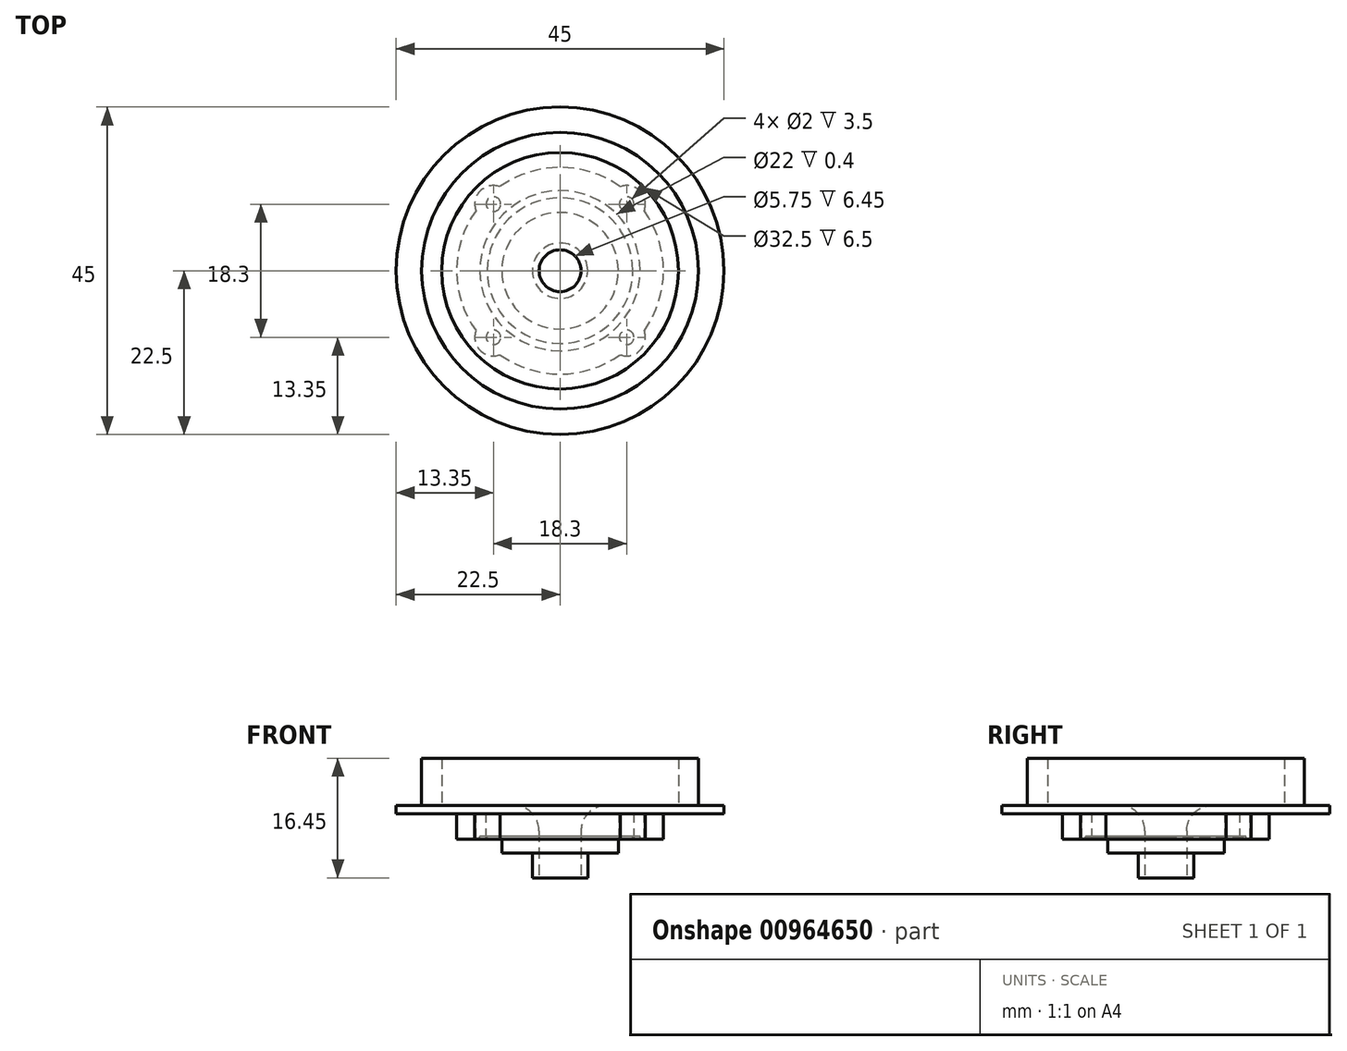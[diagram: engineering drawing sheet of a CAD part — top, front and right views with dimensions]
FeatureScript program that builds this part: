
annotation { "Feature Type Name" : "Feature", "Feature Type Description" : "" }
export const myFeature = defineFeature(function(context is Context, id is Id, definition is map)
    precondition{}
    {
        {
            var Q0;
            Q0=qCreatedBy(makeId("Top.planeOp"),FACE);
            var sketch = newSketch(context, id + "F0", { "sketchPlane" : qUnion([Q0])});
            skCircle(sketch, "E0", {"center": v(0, 0) * mm, "radius": 22.5 * mm});
            skCircle(sketch, "E1", {"center": v(0, 0) * mm, "radius": 19 * mm});
            skCircle(sketch, "E2", {"center": v(0, 0) * mm, "radius": 16.25 * mm});
            skCircle(sketch, "E3", {"center": v(0, 0) * mm, "radius": 6.4 * mm});
            skArc(sketch, "E4", {"start": v(-8.26, -11.55) * mm, "mid": v(0, -14.2) * mm, "end": v(8.26, -11.55) * mm});
            skCircle(sketch, "E5", {"center": v(0, 0) * mm, "radius": 11 * mm});
            skCircle(sketch, "E6", {"center": v(0, 0) * mm, "radius": 10 * mm});
            skCircle(sketch, "E7", {"center": v(0, 0) * mm, "radius": 8 * mm});
            skCircle(sketch, "E8", {"center": v(0, 0) * mm, "radius": 3.8 * mm});
            skCircle(sketch, "E9", {"center": v(0, 0) * mm, "radius": 2.88 * mm});
            skLineSegment(sketch, "E10.bottom", {"start": v(9.15, 9.15) * mm, "end": v(-9.15, 9.15) * mm, "construction": true});
            skLineSegment(sketch, "E10.top", {"start": v(9.15, -9.15) * mm, "end": v(-9.15, -9.15) * mm, "construction": true});
            skLineSegment(sketch, "E10.left", {"start": v(9.15, 9.15) * mm, "end": v(9.15, -9.15) * mm, "construction": true});
            skLineSegment(sketch, "E10.right", {"start": v(-9.15, 9.15) * mm, "end": v(-9.15, -9.15) * mm, "construction": true});
            skCircle(sketch, "E11", {"center": v(-9.15, 9.15) * mm, "radius": 1 * mm});
            skCircle(sketch, "E12", {"center": v(9.15, 9.15) * mm, "radius": 1 * mm});
            skCircle(sketch, "E13", {"center": v(9.15, -9.15) * mm, "radius": 1 * mm});
            skCircle(sketch, "E14", {"center": v(-9.15, -9.15) * mm, "radius": 1 * mm});
            skLineSegment(sketch, "E15.bottom", {"start": v(10.96, 10.96) * mm, "end": v(-10.96, 10.96) * mm, "construction": true});
            skLineSegment(sketch, "E15.top", {"start": v(10.96, -10.96) * mm, "end": v(-10.96, -10.96) * mm, "construction": true});
            skLineSegment(sketch, "E15.left", {"start": v(10.96, 10.96) * mm, "end": v(10.96, -10.96) * mm, "construction": true});
            skLineSegment(sketch, "E15.right", {"start": v(-10.96, 10.96) * mm, "end": v(-10.96, -10.96) * mm, "construction": true});
            skLineSegment(sketch, "E16", {"start": v(-10.96, 10.96) * mm, "end": v(10.96, -10.96) * mm, "construction": true});
            skArc(sketch, "E17", {"start": v(-8.26, 11.55) * mm, "mid": v(-10.96, 10.96) * mm, "end": v(-11.55, 8.26) * mm});
            skArc(sketch, "E18", {"start": v(11.55, 8.26) * mm, "mid": v(10.96, 10.96) * mm, "end": v(8.26, 11.55) * mm});
            skArc(sketch, "E19", {"start": v(8.26, -11.55) * mm, "mid": v(10.96, -10.96) * mm, "end": v(11.55, -8.26) * mm});
            skArc(sketch, "E20.trimOffspring", {"start": v(-11.55, -8.26) * mm, "mid": v(-10.96, -10.96) * mm, "end": v(-8.26, -11.55) * mm});
            skArc(sketch, "E21.trimOffspring", {"start": v(11.55, -8.26) * mm, "mid": v(14.2, 0) * mm, "end": v(11.55, 8.26) * mm});
            skArc(sketch, "E22.trimOffspring", {"start": v(8.26, 11.55) * mm, "mid": v(0, 14.2) * mm, "end": v(-8.26, 11.55) * mm});
            skArc(sketch, "E23.trimOffspring", {"start": v(-11.55, 8.26) * mm, "mid": v(-14.2, 0) * mm, "end": v(-11.55, -8.26) * mm});
            skSolve(sketch);
        }
        {
            var Q0;
            Q0=makeQuery(id+"F0.imprint","IMPRINT",FACE,{"disambiguationData":[TD([[makeQuery(id+"F0.imprint","IMPRINT",EDGE,{"derivedFrom":sQuery(id+"F0.wireOp",EDGE,"E0")}),1.0]])]});
            var Q1;
            Q1=makeQuery(id+"F0.imprint","IMPRINT",FACE,{"disambiguationData":[TD([[makeQuery(id+"F0.imprint","IMPRINT",EDGE,{"derivedFrom":sQuery(id+"F0.wireOp",EDGE,"E1")}),1.0]])]});
            var Q2;
            Q2=makeQuery(id+"F0.imprint","IMPRINT",FACE,{"disambiguationData":[TD([[makeQuery(id+"F0.imprint","IMPRINT",EDGE,{"derivedFrom":sQuery(id+"F0.wireOp",EDGE,"E2")}),1.0]])]});
            var Q3;
            Q3=makeQuery(id+"F0.imprint","IMPRINT",FACE,{"disambiguationData":[TD([[makeQuery(id+"F0.imprint","IMPRINT",EDGE,{"derivedFrom":sQuery(id+"F0.wireOp",EDGE,"E4")}),1.0]])]});
            var Q4;
            Q4=makeQuery(id+"F0.imprint","IMPRINT",FACE,{"disambiguationData":[TD([[makeQuery(id+"F0.imprint","IMPRINT",EDGE,{"derivedFrom":sQuery(id+"F0.wireOp",EDGE,"E5")}),1.0]])]});
            var Q5;
            Q5=makeQuery(id+"F0.imprint","IMPRINT",FACE,{"disambiguationData":[TD([[makeQuery(id+"F0.imprint","IMPRINT",EDGE,{"derivedFrom":sQuery(id+"F0.wireOp",EDGE,"E6")}),1.0]])]});
            var Q6;
            Q6=makeQuery(id+"F0.imprint","IMPRINT",FACE,{"disambiguationData":[TD([[makeQuery(id+"F0.imprint","IMPRINT",EDGE,{"derivedFrom":sQuery(id+"F0.wireOp",EDGE,"E3")}),-1.0]])]});
            var Q7;
            Q7=makeQuery(id+"F0.imprint","IMPRINT",FACE,{"disambiguationData":[TD([[makeQuery(id+"F0.imprint","IMPRINT",EDGE,{"derivedFrom":sQuery(id+"F0.wireOp",EDGE,"E11")}),1.0]])]});
            var Q8;
            Q8=makeQuery(id+"F0.imprint","IMPRINT",FACE,{"disambiguationData":[TD([[makeQuery(id+"F0.imprint","IMPRINT",EDGE,{"derivedFrom":sQuery(id+"F0.wireOp",EDGE,"E12")}),1.0]])]});
            var Q9;
            Q9=makeQuery(id+"F0.imprint","IMPRINT",FACE,{"disambiguationData":[TD([[makeQuery(id+"F0.imprint","IMPRINT",EDGE,{"derivedFrom":sQuery(id+"F0.wireOp",EDGE,"E13")}),1.0]])]});
            var Q10;
            Q10=makeQuery(id+"F0.imprint","IMPRINT",FACE,{"disambiguationData":[TD([[makeQuery(id+"F0.imprint","IMPRINT",EDGE,{"derivedFrom":sQuery(id+"F0.wireOp",EDGE,"E14")}),1.0]])]});
            var Q11;
            Q11=makeQuery(id+"F0.imprint","IMPRINT",FACE,{"disambiguationData":[TD([[makeQuery(id+"F0.imprint","IMPRINT",EDGE,{"derivedFrom":sQuery(id+"F0.wireOp",EDGE,"E3")}),1.0]])]});
            var Q12;
            Q12=makeQuery(id+"F0.imprint","IMPRINT",FACE,{"disambiguationData":[TD([[makeQuery(id+"F0.imprint","IMPRINT",EDGE,{"derivedFrom":sQuery(id+"F0.wireOp",EDGE,"E8")}),1.0]])]});
            extrude(context, id + "F1", {"entities" : qUnion([Q0, Q1, Q2, Q3, Q4, Q5, Q6, Q7, Q8, Q9, Q10, Q11, Q12]), "depth" : 1.15 * mm, "offsetDistance" : 25 * mm});
        }
        {
            var Q0;
            Q0=makeQuery(id+"F0.imprint","IMPRINT",FACE,{"disambiguationData":[TD([[makeQuery(id+"F0.imprint","IMPRINT",EDGE,{"derivedFrom":sQuery(id+"F0.wireOp",EDGE,"E1")}),1.0]])]});
            extrude(context, id + "F2", {"entities" : qUnion([Q0]), "operationType" : NewBodyOperationType.ADD, "depth" : 7.65 * mm, "offsetDistance" : 25 * mm});
        }
        {
            var Q0;
            Q0=makeQuery(id+"F0.imprint","IMPRINT",FACE,{"disambiguationData":[TD([[makeQuery(id+"F0.imprint","IMPRINT",EDGE,{"derivedFrom":sQuery(id+"F0.wireOp",EDGE,"E4")}),1.0]])]});
            var Q1;
            Q1=makeQuery(id+"F0.imprint","IMPRINT",FACE,{"disambiguationData":[TD([[makeQuery(id+"F0.imprint","IMPRINT",EDGE,{"derivedFrom":sQuery(id+"F0.wireOp",EDGE,"E6")}),1.0]])]});
            extrude(context, id + "F3", {"entities" : qUnion([Q0, Q1]), "operationType" : NewBodyOperationType.ADD, "oppositeDirection" : true, "depth" : 3.5 * mm, "offsetDistance" : 25 * mm});
        }
        {
            var Q0;
            Q0=makeQuery(id+"F0.imprint","IMPRINT",FACE,{"disambiguationData":[TD([[makeQuery(id+"F0.imprint","IMPRINT",EDGE,{"derivedFrom":sQuery(id+"F0.wireOp",EDGE,"E5")}),1.0]])]});
            extrude(context, id + "F4", {"entities" : qUnion([Q0]), "operationType" : NewBodyOperationType.ADD, "oppositeDirection" : true, "depth" : 3.1 * mm, "offsetDistance" : 25 * mm});
        }
        {
            var Q0;
            Q0=makeQuery(id+"F0.imprint","IMPRINT",FACE,{"disambiguationData":[TD([[makeQuery(id+"F0.imprint","IMPRINT",EDGE,{"derivedFrom":sQuery(id+"F0.wireOp",EDGE,"E3")}),-1.0]])]});
            var Q1;
            Q1=makeQuery(id+"F0.imprint","IMPRINT",FACE,{"disambiguationData":[TD([[makeQuery(id+"F0.imprint","IMPRINT",EDGE,{"derivedFrom":sQuery(id+"F0.wireOp",EDGE,"E3")}),1.0]])]});
            extrude(context, id + "F5", {"entities" : qUnion([Q0, Q1]), "operationType" : NewBodyOperationType.ADD, "oppositeDirection" : true, "depth" : 5.4 * mm, "offsetDistance" : 25 * mm});
        }
        {
            var Q0;
            Q0=makeQuery(id+"F0.imprint","IMPRINT",FACE,{"disambiguationData":[TD([[makeQuery(id+"F0.imprint","IMPRINT",EDGE,{"derivedFrom":sQuery(id+"F0.wireOp",EDGE,"E8")}),1.0]])]});
            extrude(context, id + "F6", {"entities" : qUnion([Q0]), "operationType" : NewBodyOperationType.ADD, "oppositeDirection" : true, "depth" : 8.8 * mm, "offsetDistance" : 25 * mm});
        }
        {
            var Q0;
            Q0=makeQuery(id+"F1.opExtrude","CAP_EDGE",EDGE,{"disambiguationData":[OSD([sQuery(id+"F0.wireOp",EDGE,"E9")])],"isStart":false});
            fillet(context, id + "F7", {"entities" : qUnion([Q0]), "radius" : 3.5 * mm, "tangentPropagation" : true, "allowEdgeOverflow" : false});
        }
    });
